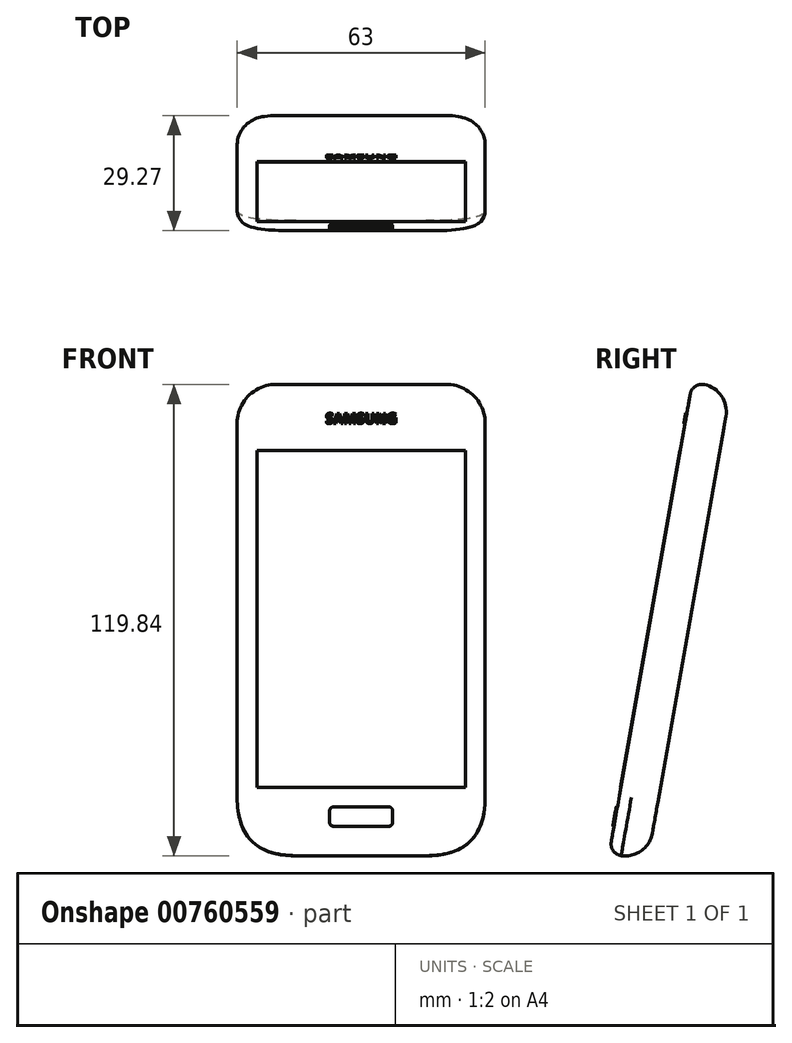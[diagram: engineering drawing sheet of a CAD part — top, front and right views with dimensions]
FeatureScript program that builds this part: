
annotation { "Feature Type Name" : "Feature", "Feature Type Description" : "" }
export const myFeature = defineFeature(function(context is Context, id is Id, definition is map)
    precondition{}
    {
        {
            var Q0;
            Q0=qCreatedBy(makeId("Top.planeOp"),FACE);
            var sketch = newSketch(context, id + "F0", { "sketchPlane" : qUnion([Q0])});
            skLineSegment(sketch, "E0.bottom", {"start": v(-31.5, 4.95) * mm, "end": v(31.5, 4.95) * mm});
            skLineSegment(sketch, "E0.top", {"start": v(-31.5, -4.95) * mm, "end": v(31.5, -4.95) * mm});
            skLineSegment(sketch, "E0.left", {"start": v(-31.5, 4.95) * mm, "end": v(-31.5, -4.95) * mm});
            skLineSegment(sketch, "E0.right", {"start": v(31.5, 4.95) * mm, "end": v(31.5, -4.95) * mm});
            skSolve(sketch);
        }
        {
            var Q0;
            Q0 = qSketchRegion(id + "F0", true);
            extrude(context, id + "F1", {"entities" : qUnion([Q0]), "depth" : 121.55 * mm, "offsetDistance" : 25 * mm});
        }
        {
            var Q0;
            Q0=makeQuery(id+"F1.opExtrude","CAP_EDGE",EDGE,{"disambiguationData":[OSD([sQuery(id+"F0.wireOp",EDGE,"E0.right")])],"isStart":true});
            var Q1;
            Q1=makeQuery(id+"F1.opExtrude","CAP_EDGE",EDGE,{"disambiguationData":[OSD([sQuery(id+"F0.wireOp",EDGE,"E0.left")])],"isStart":true});
            fillet(context, id + "F2", {"entities" : qUnion([Q0, Q1]), "radius" : 15 * mm, "tangentPropagation" : true, "rho" : 0.5, "crossSection" : FilletCrossSection.CONIC, "allowEdgeOverflow" : false});
        }
        {
            var Q0;
            Q0=makeQuery(id+"F1.opExtrude","CAP_EDGE",EDGE,{"disambiguationData":[OSD([sQuery(id+"F0.wireOp",EDGE,"E0.right")])],"isStart":false});
            var Q1;
            Q1=makeQuery(id+"F1.opExtrude","CAP_EDGE",EDGE,{"disambiguationData":[OSD([sQuery(id+"F0.wireOp",EDGE,"E0.left")])],"isStart":false});
            fillet(context, id + "F3", {"entities" : qUnion([Q0, Q1]), "radius" : 10 * mm, "tangentPropagation" : true, "allowEdgeOverflow" : false});
        }
        {
            var Q0;
            Q0=makeQuery(id+"F1.opExtrude","SWEPT_FACE",FACE,{"disambiguationData":[OSD([sQuery(id+"F0.wireOp",EDGE,"E0.top")])]});
            var sketch = newSketch(context, id + "F4", { "sketchPlane" : qUnion([Q0])});
            skLineSegment(sketch, "E1.bottom", {"start": v(-7, 12) * mm, "end": v(7, 12) * mm});
            skLineSegment(sketch, "E1.top", {"start": v(-7, 7) * mm, "end": v(7, 7) * mm});
            skLineSegment(sketch, "E1.left", {"start": v(-8, 11) * mm, "end": v(-8, 8) * mm});
            skLineSegment(sketch, "E1.right", {"start": v(8, 11) * mm, "end": v(8, 8) * mm});
            skPoint(sketch, "E2.visualSharp", {"position": v(-8, 12) * mm});
            skArc(sketch, "E2.filletArc", {"start": v(-7, 12) * mm, "mid": v(-7.7, 11.7) * mm, "end": v(-8, 11) * mm});
            skPoint(sketch, "E3.visualSharp", {"position": v(-8, 7) * mm});
            skArc(sketch, "E3.filletArc", {"start": v(-8, 8) * mm, "mid": v(-7.7, 7.3) * mm, "end": v(-7, 7) * mm});
            skPoint(sketch, "E4.visualSharp", {"position": v(8, 7) * mm});
            skArc(sketch, "E4.filletArc", {"start": v(7, 7) * mm, "mid": v(7.7, 7.3) * mm, "end": v(8, 8) * mm});
            skPoint(sketch, "E5.visualSharp", {"position": v(8, 12) * mm});
            skArc(sketch, "E5.filletArc", {"start": v(8, 11) * mm, "mid": v(7.7, 11.7) * mm, "end": v(7, 12) * mm});
            skSolve(sketch);
        }
        {
            var Q0;
            Q0 = qSketchRegion(id + "F4", true);
            extrude(context, id + "F5", {"entities" : qUnion([Q0]), "operationType" : NewBodyOperationType.ADD, "depth" : 0.3 * mm, "offsetDistance" : 25 * mm});
        }
        {
            var Q0;
            Q0=makeQuery(id+"F2.opFillet","BLEND_EDGE",EDGE,{"blendedFrom":[makeQuery(id+"F1.opExtrude","CAP_EDGE",EDGE,{"disambiguationData":[OSD([sQuery(id+"F0.wireOp",EDGE,"E0.right")])],"isStart":true}),makeQuery(id+"F1.opExtrude","SWEPT_FACE",FACE,{"disambiguationData":[OSD([sQuery(id+"F0.wireOp",EDGE,"E0.bottom")])]})],"blendedInto":[makeQuery(id+"F1.opExtrude","SWEPT_FACE",FACE,{"disambiguationData":[OSD([sQuery(id+"F0.wireOp",EDGE,"E0.bottom")])]})]});
            fillet(context, id + "F6", {"entities" : qUnion([Q0]), "radius" : 7 * mm, "tangentPropagation" : true, "allowEdgeOverflow" : false});
        }
        {
            var Q0;
            Q0=makeQuery(id+"F2.opFillet","BLEND_EDGE",EDGE,{"blendedFrom":[makeQuery(id+"F1.opExtrude","CAP_EDGE",EDGE,{"disambiguationData":[OSD([sQuery(id+"F0.wireOp",EDGE,"E0.right")])],"isStart":true}),makeQuery(id+"F1.opExtrude","SWEPT_FACE",FACE,{"disambiguationData":[OSD([sQuery(id+"F0.wireOp",EDGE,"E0.top")])]})],"blendedInto":[makeQuery(id+"F1.opExtrude","SWEPT_FACE",FACE,{"disambiguationData":[OSD([sQuery(id+"F0.wireOp",EDGE,"E0.top")])]})]});
            fillet(context, id + "F7", {"entities" : qUnion([Q0]), "radius" : 3 * mm, "tangentPropagation" : true, "allowEdgeOverflow" : false});
        }
        {
            var Q0;
            Q0=makeQuery(id+"F1.opExtrude","SWEPT_FACE",FACE,{"disambiguationData":[OSD([sQuery(id+"F0.wireOp",EDGE,"E0.top")])]});
            var sketch = newSketch(context, id + "F8", { "sketchPlane" : qUnion([Q0])});
            skText(sketch, "E6", { "text": "SAMSUNG", "fontName": "OpenSans-Bold.ttf"});
            const initialGuessF8  = {"E6": [-0.009, 0.11096, 1, 0, 0.00259]};
            skSetInitialGuess(sketch, initialGuessF8);
            skSolve(sketch);
        }
        {
            var Q0;
            Q0 = qSketchRegion(id + "F8", true);
            extrude(context, id + "F9", {"entities" : qUnion([Q0]), "operationType" : NewBodyOperationType.ADD, "depth" : 0.3 * mm, "offsetDistance" : 25 * mm});
        }
        {
            var Q0;
            Q0=makeQuery(id+"F1.opExtrude","SWEPT_BODY",BODY,{"disambiguationData":[OSD([sQuery(id+"F0.wireOp",EDGE,"E0.bottom"),sQuery(id+"F0.wireOp",EDGE,"E0.top"),sQuery(id+"F0.wireOp",EDGE,"E0.left"),sQuery(id+"F0.wireOp",EDGE,"E0.right")])]});
            transform(context, id + "F10", {"entities" : qUnion([Q0]), "transformType" : TransformType.TRANSLATION_3D, "dx" : 37.5 * mm, "dy" : 0 * mm, "dz" : 30 * mm, "makeCopy" : false});
        }
        {
            var Q0;
            Q0=qCreatedBy(makeId("Front.planeOp"),FACE);
            var sketch = newSketch(context, id + "F11", { "sketchPlane" : qUnion([Q0])});
            skLineSegment(sketch, "E7", {"start": v(-100, 30) * mm, "end": v(100, 30) * mm});
            skSolve(sketch);
        }
        {
            var Q0;
            Q0=makeQuery(id+"F1.opExtrude","SWEPT_BODY",BODY,{"disambiguationData":[OSD([sQuery(id+"F0.wireOp",EDGE,"E0.bottom"),sQuery(id+"F0.wireOp",EDGE,"E0.top"),sQuery(id+"F0.wireOp",EDGE,"E0.left"),sQuery(id+"F0.wireOp",EDGE,"E0.right")])]});
            var Q1;
            Q1=sQuery(id+"F11.wireOp",EDGE,"E7");
            var Q2;
            Q2=sQuery(id+"F11.wireOp",EDGE,"E7");
            transform(context, id + "F12", {"entities" : qUnion([Q0]), "transformType" : TransformType.ROTATION, "transformAxis" : qUnion([Q2]), "angle" : 10 * degree, "oppositeDirection" : true, "makeCopy" : false});
        }
        {
            var Q0;
            {var subQ1=sQuery(id+"F0.wireOp",EDGE,"E0.top");var subQ3=makeQuery(id+"F1.opExtrude","SWEPT_FACE",FACE,{"disambiguationData":[OSD([subQ1])]});var subQ4=subQ3;Q0=makeQuery(id+"F9.boolean.opBoolean","SPLIT",FACE,{"disambiguationData":[TD([makeQuery(id+"F5.opExtrude","SWEPT_FACE",FACE,{"disambiguationData":[OSD([sQuery(id+"F4.wireOp",EDGE,"E1.bottom")])]})])],"derivedFrom":subQ4});}
            var sketch = newSketch(context, id + "F13", { "sketchPlane" : qUnion([Q0])});
            skLineSegment(sketch, "E8.bottom", {"start": v(11, 133.55) * mm, "end": v(64, 133.55) * mm});
            skLineSegment(sketch, "E8.top", {"start": v(11, 46.55) * mm, "end": v(64, 46.55) * mm});
            skLineSegment(sketch, "E8.left", {"start": v(11, 133.55) * mm, "end": v(11, 46.55) * mm});
            skLineSegment(sketch, "E8.right", {"start": v(64, 133.55) * mm, "end": v(64, 46.55) * mm});
            skLineSegment(sketch, "E9", {"start": v(37.5, 148.1) * mm, "end": v(37.5, 32.55) * mm, "construction": true});
            skSolve(sketch);
        }
        {
            var Q0;
            Q0 = qSketchRegion(id + "F13", true);
            extrude(context, id + "F14", {"entities" : qUnion([Q0]), "depth" : 0.1 * mm, "offsetDistance" : 25 * mm});
        }
    });
